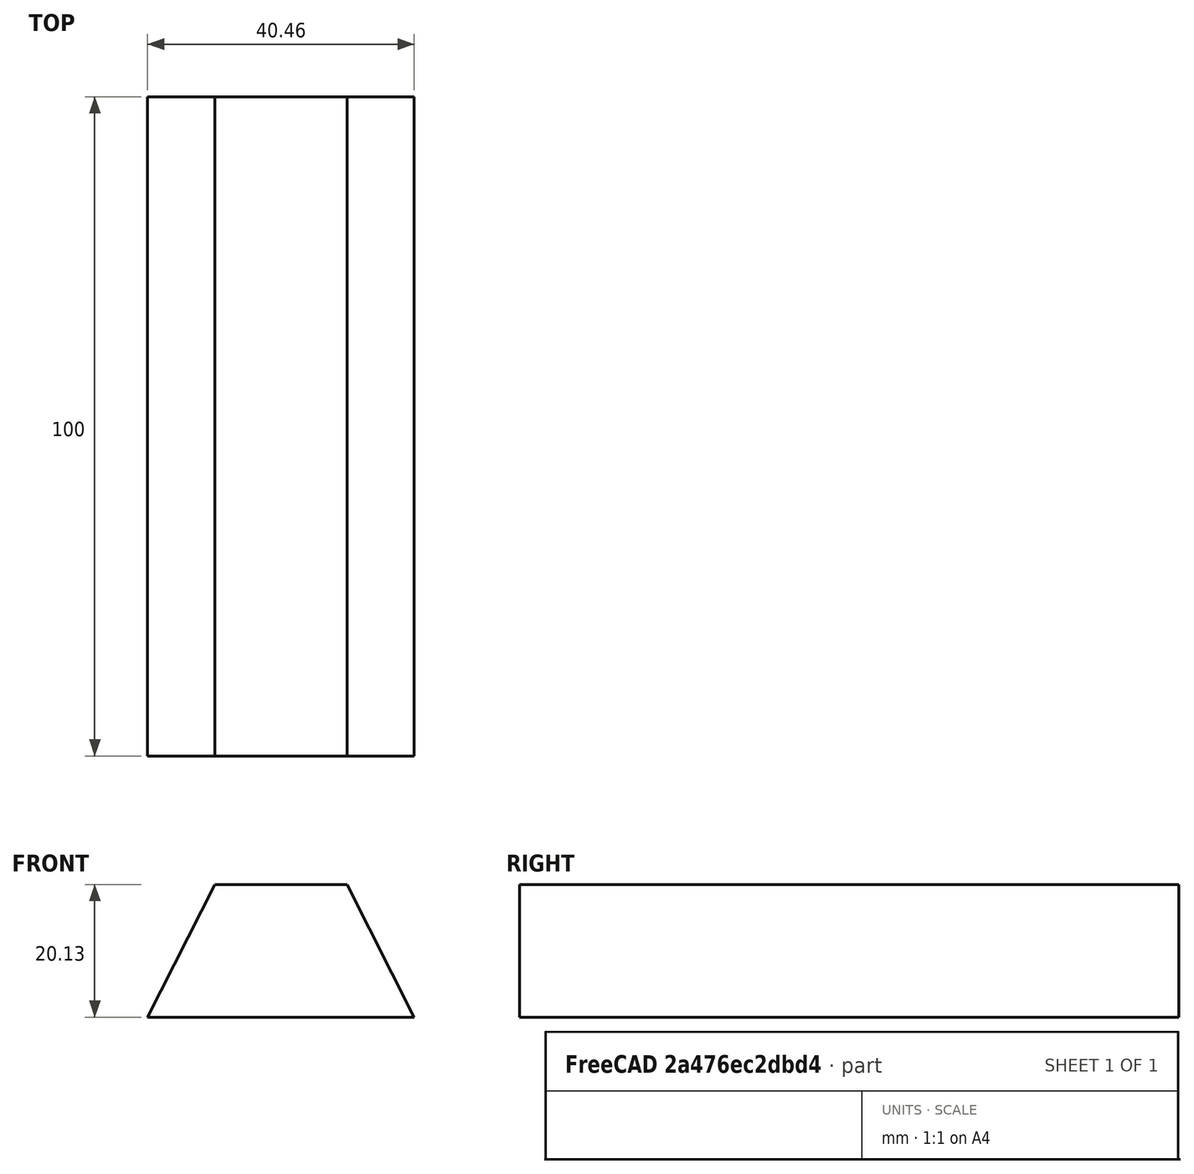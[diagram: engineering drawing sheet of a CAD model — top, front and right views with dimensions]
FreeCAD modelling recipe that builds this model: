
FCSTD DOCUMENT  (FreeCAD 0.21R33694 (Git))
Label: OJT1_T016_Figura1
License: All rights reserved
LicenseURL: https://en.wikipedia.org/wiki/All_rights_reserved
objects: Sketcher::SketchObject×1, PartDesign::Pad×1, PartDesign::Body×1
note: 4 computed .brp shape members not serialized (recipe doc carries the construction recipe); baked Part::Feature solids carry a one-line shape summary decoded from their .brp

FEATURE [Sketcher::SketchObject] Sketch
  FullyConstrained = false
  MapMode = 5
  Placement = pos=(0,0,0) rot=(1,0,0;1.5708rad)
  Support = -> [XZ_Plane]
  sketch-geometry (4):
    g0: LineSegment StartX=-20.2268 StartY=0 StartZ=0 EndX=-10.0189 EndY=20.1323 EndZ=0
    g1: LineSegment StartX=-10.0189 StartY=20.1323 StartZ=0 EndX=10.0189 EndY=20.1323 EndZ=0
    g2: LineSegment StartX=10.0189 StartY=20.1323 StartZ=0 EndX=20.2268 EndY=0 EndZ=0
    g3: LineSegment StartX=20.2268 StartY=0 StartZ=0 EndX=-20.2268 EndY=0 EndZ=0
  constraints (7):
    c: PointOnObject(g0,g-1)
    c: Coincident(g1,g0)
    c: Horizontal(g1)
    c: Coincident(g2,g1)
    c: PointOnObject(g2,g-1)
    c: Coincident(g3,g0)
    c: Horizontal(g3)
FEATURE [PartDesign::Pad] Pad
  Direction = (0,-1,2e-16)
  Length = 100
  Length2 = 10
  Placement = pos=(0,0,0) rot=(1,0,0;1.5708rad)
  Profile = -> Sketch
  ReferenceAxis = -> Sketch [N_Axis]
  Type = 0
FEATURE [PartDesign::Body] Body
  Group = -> [Sketch,Pad]
  Origin = -> Origin
  Tip = -> Pad
